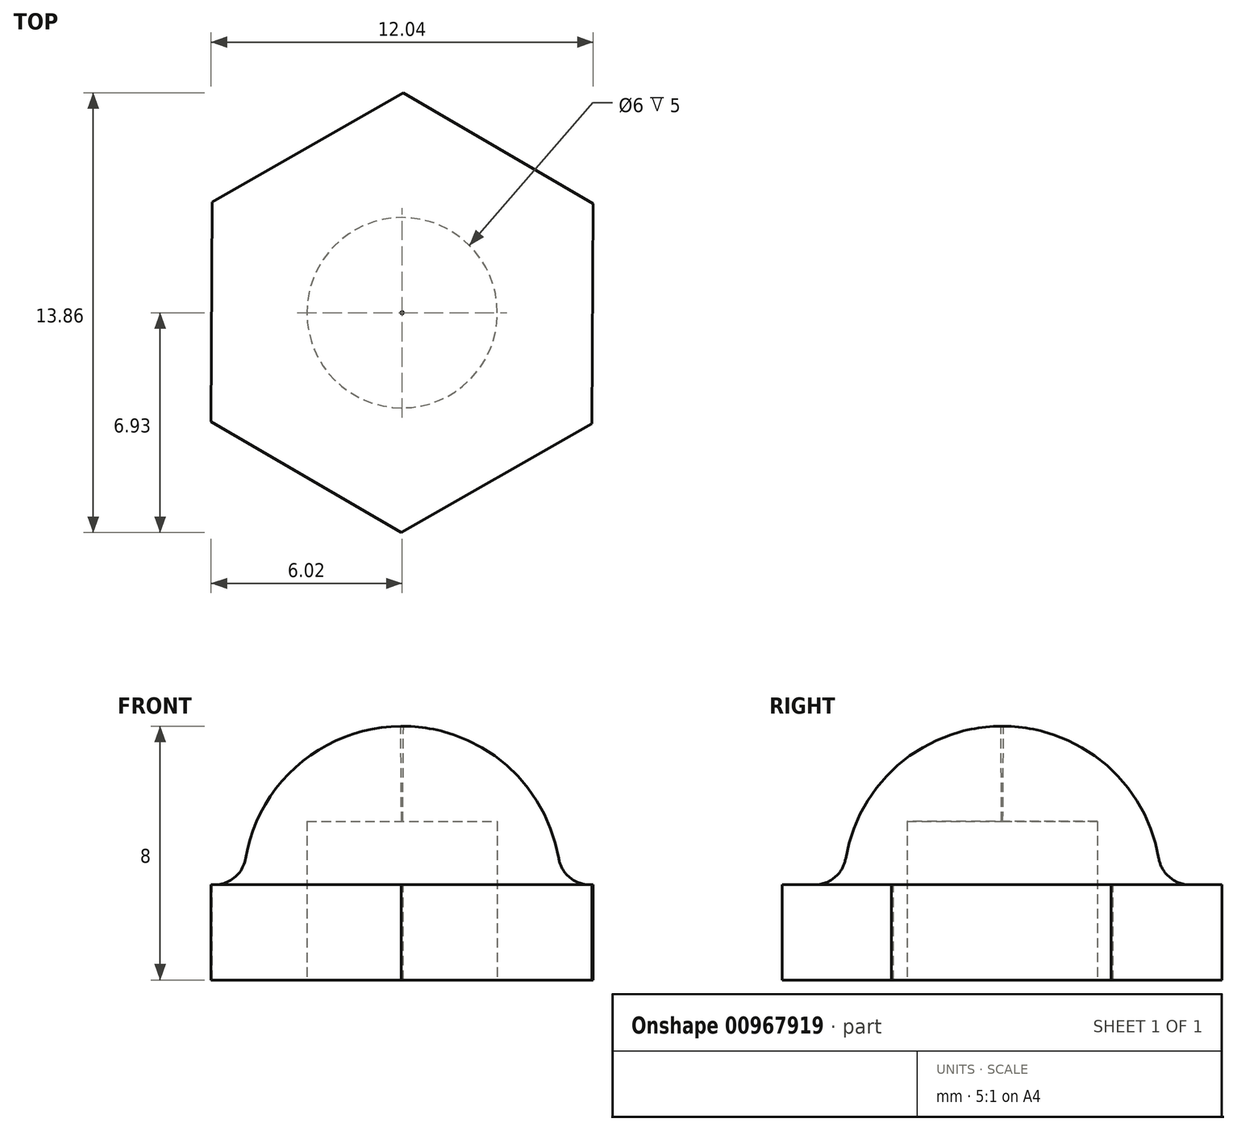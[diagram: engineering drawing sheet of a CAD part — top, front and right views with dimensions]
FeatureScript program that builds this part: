
annotation { "Feature Type Name" : "Feature", "Feature Type Description" : "" }
export const myFeature = defineFeature(function(context is Context, id is Id, definition is map)
    precondition{}
    {
        {
            var Q0;
            Q0=qCreatedBy(makeId("Top.planeOp"),FACE);
            var sketch = newSketch(context, id + "F0", { "sketchPlane" : qUnion([Q0])});
            skCircle(sketch, "E0.cCircle", {"center": v(0, 0) * mm, "radius": 6 * mm, "construction": true});
            skLineSegment(sketch, "E0.0", {"start": v(-5.98, 3.5) * mm, "end": v(0.03, 6.93) * mm});
            skLineSegment(sketch, "E0.1", {"start": v(0.03, 6.93) * mm, "end": v(6.02, 3.43) * mm});
            skLineSegment(sketch, "E0.2", {"start": v(6.02, 3.43) * mm, "end": v(5.98, -3.5) * mm});
            skLineSegment(sketch, "E0.3", {"start": v(5.98, -3.5) * mm, "end": v(-0.03, -6.93) * mm});
            skLineSegment(sketch, "E0.4", {"start": v(-0.03, -6.93) * mm, "end": v(-6.02, -3.43) * mm});
            skLineSegment(sketch, "E0.5", {"start": v(-6.02, -3.43) * mm, "end": v(-5.98, 3.5) * mm});
            skPoint(sketch, "E0.0.midPoint", {"position": v(-2.97, 5.21) * mm});
            skCircle(sketch, "E1", {"center": v(0, 0) * mm, "radius": 6 * mm});
            skCircle(sketch, "E2", {"center": v(0, 0) * mm, "radius": 5 * mm});
            skSolve(sketch);
        }
        {
            var Q0;
            Q0=qCreatedBy(makeId("Right.planeOp"),FACE);
            var sketch = newSketch(context, id + "F1", { "sketchPlane" : qUnion([Q0])});
            skArc(sketch, "E3", {"start": v(4.93, 0.83) * mm, "mid": v(0, 5) * mm, "end": v(-4.93, 0.83) * mm});
            skLineSegment(sketch, "E4", {"start": v(5.92, 0) * mm, "end": v(6, 0) * mm});
            skPoint(sketch, "E5.visualSharp", {"position": v(5, 0) * mm});
            skArc(sketch, "E5.filletArc", {"start": v(4.93, 0.83) * mm, "mid": v(5.27, 0.24) * mm, "end": v(5.92, 0) * mm});
            skLineSegment(sketch, "E6", {"start": v(-5.91, 0) * mm, "end": v(-6, 0) * mm});
            skPoint(sketch, "E7.visualSharp", {"position": v(-5, 0) * mm});
            skArc(sketch, "E7.filletArc", {"start": v(-5.91, 0) * mm, "mid": v(-5.27, 0.24) * mm, "end": v(-4.93, 0.83) * mm});
            skLineSegment(sketch, "E8", {"start": v(-5.91, 0) * mm, "end": v(6, 0) * mm});
            skLineSegment(sketch, "E9", {"start": v(0, 0) * mm, "end": v(0.04, 5) * mm});
            skPoint(sketch, "E9.endSnap0", {"position": v(0.04, 0) * mm});
            skSolve(sketch);
        }
        {
            var Q0;
            {var subQ0=sQuery(id+"F0.wireOp",EDGE,"E0.5");var subQ1=sQuery(id+"F0.wireOp",EDGE,"E0.0");var subQ2=makeQuery(id+"F0.imprint","INTERSECT",VERTEX,{"derivedFrom":[subQ1,subQ0]});Q0=makeQuery(id+"F0.imprint","IMPRINT",FACE,{"disambiguationData":[TD([[makeQuery(id+"F0.imprint","IMPRINT",EDGE,{"disambiguationData":[TD([[subQ2,-1.0]])],"derivedFrom":subQ1}),-1.0]])]});}
            var Q1;
            {var subQ0=sQuery(id+"F0.wireOp",EDGE,"E0.1");var subQ1=sQuery(id+"F0.wireOp",EDGE,"E0.0");var subQ2=makeQuery(id+"F0.imprint","INTERSECT",VERTEX,{"derivedFrom":[subQ1,subQ0]});Q1=makeQuery(id+"F0.imprint","IMPRINT",FACE,{"disambiguationData":[TD([[makeQuery(id+"F0.imprint","IMPRINT",EDGE,{"disambiguationData":[TD([[subQ2,1.0]])],"derivedFrom":subQ1}),-1.0]])]});}
            var Q2;
            {var subQ0=sQuery(id+"F0.wireOp",EDGE,"E0.2");var subQ1=sQuery(id+"F0.wireOp",EDGE,"E0.1");var subQ2=makeQuery(id+"F0.imprint","INTERSECT",VERTEX,{"derivedFrom":[subQ1,subQ0]});Q2=makeQuery(id+"F0.imprint","IMPRINT",FACE,{"disambiguationData":[TD([[makeQuery(id+"F0.imprint","IMPRINT",EDGE,{"disambiguationData":[TD([[subQ2,1.0]])],"derivedFrom":subQ1}),-1.0]])]});}
            var Q3;
            {var subQ0=sQuery(id+"F0.wireOp",EDGE,"E0.3");var subQ1=sQuery(id+"F0.wireOp",EDGE,"E0.2");var subQ2=makeQuery(id+"F0.imprint","INTERSECT",VERTEX,{"derivedFrom":[subQ1,subQ0]});Q3=makeQuery(id+"F0.imprint","IMPRINT",FACE,{"disambiguationData":[TD([[makeQuery(id+"F0.imprint","IMPRINT",EDGE,{"disambiguationData":[TD([[subQ2,1.0]])],"derivedFrom":subQ1}),-1.0]])]});}
            var Q4;
            {var subQ0=sQuery(id+"F0.wireOp",EDGE,"E0.4");var subQ1=sQuery(id+"F0.wireOp",EDGE,"E0.3");var subQ2=makeQuery(id+"F0.imprint","INTERSECT",VERTEX,{"derivedFrom":[subQ1,subQ0]});Q4=makeQuery(id+"F0.imprint","IMPRINT",FACE,{"disambiguationData":[TD([[makeQuery(id+"F0.imprint","IMPRINT",EDGE,{"disambiguationData":[TD([[subQ2,1.0]])],"derivedFrom":subQ1}),-1.0]])]});}
            var Q5;
            {var subQ0=sQuery(id+"F0.wireOp",EDGE,"E0.5");var subQ1=sQuery(id+"F0.wireOp",EDGE,"E0.4");var subQ2=makeQuery(id+"F0.imprint","INTERSECT",VERTEX,{"derivedFrom":[subQ1,subQ0]});Q5=makeQuery(id+"F0.imprint","IMPRINT",FACE,{"disambiguationData":[TD([[makeQuery(id+"F0.imprint","IMPRINT",EDGE,{"disambiguationData":[TD([[subQ2,1.0]])],"derivedFrom":subQ1}),-1.0]])]});}
            var Q6;
            Q6=makeQuery(id+"F0.imprint","IMPRINT",FACE,{"disambiguationData":[TD([[makeQuery(id+"F0.imprint","IMPRINT",EDGE,{"derivedFrom":sQuery(id+"F0.wireOp",EDGE,"E2")}),-1.0]])]});
            var Q7;
            Q7=makeQuery(id+"F0.imprint","IMPRINT",FACE,{"disambiguationData":[TD([[makeQuery(id+"F0.imprint","IMPRINT",EDGE,{"derivedFrom":sQuery(id+"F0.wireOp",EDGE,"E2")}),1.0]])]});
            extrude(context, id + "F2", {"entities" : qUnion([Q0, Q1, Q2, Q3, Q4, Q5, Q6, Q7]), "oppositeDirection" : true, "depth" : 3 * mm, "offsetDistance" : 25 * mm});
        }
        {
            var Q0;
            {var subQ0=sQuery(id+"F1.wireOp",EDGE,"E5.filletArc");Q0=makeQuery(id+"F1.imprint","IMPRINT",FACE,{"disambiguationData":[TD([[makeQuery(id+"F1.imprint","IMPRINT",EDGE,{"derivedFrom":subQ0}),-1.0]])]});}
            var Q1;
            Q1=sQuery(id+"F0.wireOp",EDGE,"E2");
            revolve(context, id + "F3", {"operationType" : NewBodyOperationType.ADD, "surfaceOperationType" : NewSurfaceOperationType.NEW, "entities" : qUnion([Q0]), "axis" : qUnion([Q1]), "revolveType" : RevolveType.FULL});
        }
        {
            var Q0;
            Q0=makeQuery(id+"F2.opExtrude","CAP_FACE",FACE,{"disambiguationData":[OSD([sQuery(id+"F0.wireOp",EDGE,"E0.0"),sQuery(id+"F0.wireOp",EDGE,"E0.1"),sQuery(id+"F0.wireOp",EDGE,"E0.2"),sQuery(id+"F0.wireOp",EDGE,"E0.3"),sQuery(id+"F0.wireOp",EDGE,"E0.4"),sQuery(id+"F0.wireOp",EDGE,"E0.5"),sQuery(id+"F0.wireOp",EDGE,"E1")])],"isStart":false});
            var sketch = newSketch(context, id + "F4", { "sketchPlane" : qUnion([Q0])});
            skCircle(sketch, "E10", {"center": v(0, 0) * mm, "radius": 3 * mm});
            skSolve(sketch);
        }
        {
            var Q0;
            Q0=makeQuery(id+"F4.imprint","IMPRINT",FACE,{"disambiguationData":[TD([[makeQuery(id+"F4.imprint","IMPRINT",EDGE,{"derivedFrom":sQuery(id+"F4.wireOp",EDGE,"E10")}),1.0]])]});
            extrude(context, id + "F5", {"entities" : qUnion([Q0]), "operationType" : NewBodyOperationType.REMOVE, "oppositeDirection" : true, "depth" : 5 * mm, "offsetDistance" : 25 * mm});
        }
    });
